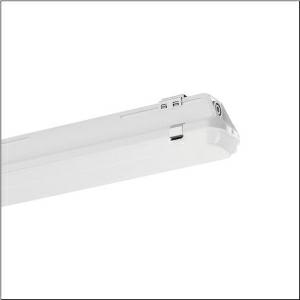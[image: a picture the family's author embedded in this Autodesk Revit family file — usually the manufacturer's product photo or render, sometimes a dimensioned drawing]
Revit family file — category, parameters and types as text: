
# Revit family: monsun_r__11_51fp108p430h_5d5d
name_source: partatom
category: Lighting Fixtures
units: mm (PartAtom-declared; Revit-internal decimal feet)

## family parameters
Cut with Voids When Loaded = No
Host = Face
Light Source = No
Part Type = Normal
Room Calculation Point = No
Round Connector Dimension = Use Diameter
Shared = No

## types (1)
- Monsun® 11 (1 x LED, 3970 lm, 22.2 W, 4000K)
    Apparent Load = 22 VA
    CIE Flux Codes = 47 77 93 94 100
    Color Rendering = 80
    Color Temperature = 4000K
    Default Elevation = 1800 mm
    Description = Monsun® 11, damp-proof luminaire, chain hanger, primary optical cover: enclosure, of PMMA, light emission: direct distribution, primary light characteristic: symmetric, installation type: suspended mounting, surface-mounted, horizontal mounting, vertical mounting, LED, rated luminous flux: 3.970lm, luminous efficacy: 179lm/W, light colour: 840, colour temperature: 4000K, control gear: ON/OFF, with terminal, 3-pole, max. 2.5mm², mains connection: 220..240V, AC, 50/60Hz, rated input power: 22W, luminaire housing, of glass-fibre reinforced polyester, uncoated, bright grey, incl. chain hanger, length: 1.590mm, width: 90mm, height: 88mm, clip for enclosure, of stainless steel (V2A), ceiling mounting element, of stainless steel (V2A), chain hanger, of stainless steel (V2A), protection rating (complete): IP66, insulation class (complete): insulation class I (protective earthing), certification: CE, ENEC, VDE, UKCA, protection symbol: D, impact resistance: IK04, permissible operating ambient temperature: -35..+40°C, standard: EN 50419, EN 60598-2-1, no direct snow, no direct sun, no direct rain, for indoor or canopied outdoor use, corresponds to IFS (International Featured Standards) requirements for safety and quality in the food industry, contact your sales advisor before using the luminaires in applications with unclear chemical exposure, large temperature fluctuations or condensation-forming humidity, LABS conformity tested according to VDMA 24364:2018-05, packaging unit: 1 piece
    Height = 89 mm
    Lamp = 1 x LED
    Lamp Light Flux = 3970 lm
    Lamp Power = 22.2 W
    Lamp count = 1
    Length = 1590 mm
    Luminous efficacy = 179 lm/W
    Manufacturer = Siteco
    ModVariant = No
    Model = 51FP108P430H
    Mounting Place = Ceiling
    Mounting Type = Surface mounted
    Number of Poles = 1
    OnlyDefault = Yes
    Power Factor = 1
    Product Name = Monsun® 11
    Product group = damp-proof luminaire
    ProductGroupID = 300
    Protection Class = Protection class I
    Protection Degree = IP 66
    RLX_Detail_Level = 1
    RLX_Emergency_Light_Flux = 0 lm
    RLX_Emergency_Type = 0
    RLX_Emergency_Type_DB = No
    RlxData = <blob elided: 88393 chars, md5=01e51f22>
    Socket = socket
    Standby Power = 0 W
    System Light Flux = 3970 lm
    System Power = 22 W
    Type Comments = Product without accessories
    Type Image = l_1349237.jpg
    URL = http://relux.com
    VarID = ---
    Voltage = 0 V
    Weight = 0.00 kg
    Width = 90 mm

## geometry (parser evidence)
native form markers: Blend x4, Sweep x13
no freeform markers — native parametric forms only
